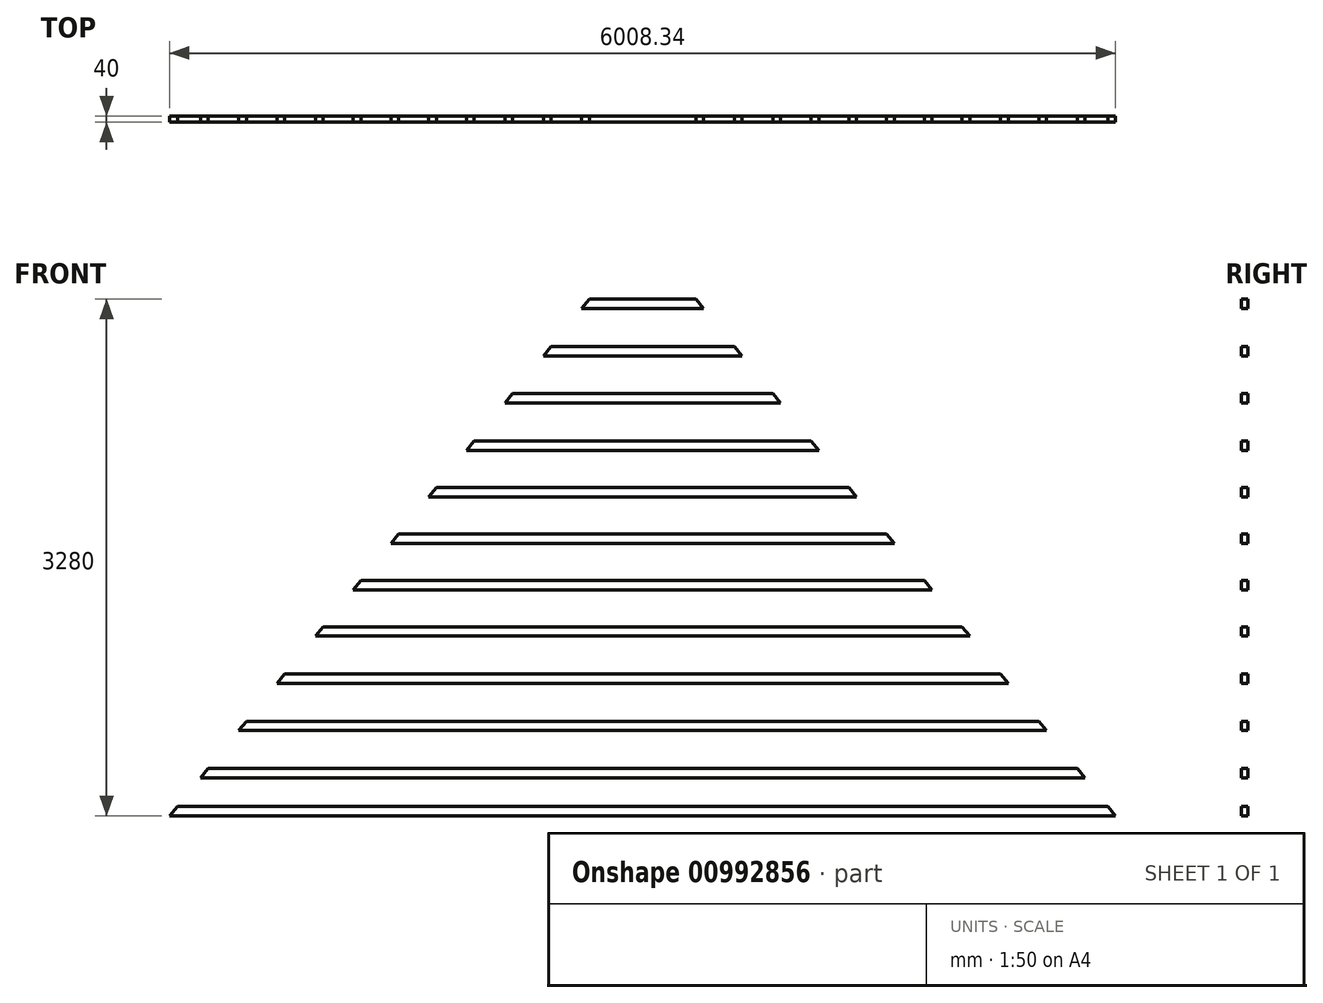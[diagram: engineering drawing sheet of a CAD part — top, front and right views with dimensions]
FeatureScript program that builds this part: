
annotation { "Feature Type Name" : "Feature", "Feature Type Description" : "" }
export const myFeature = defineFeature(function(context is Context, id is Id, definition is map)
    precondition{}
    {
        {
            var Q0;
            Q0=qCreatedBy(makeId("Front.planeOp"),FACE);
            var sketch = newSketch(context, id + "F0", { "sketchPlane" : qUnion([Q0])});
            skLineSegment(sketch, "E0", {"start": v(582.18, -714.87) * mm, "end": v(-582.6, -714.87) * mm});
            skLineSegment(sketch, "E1", {"start": v(630.94, -774.87) * mm, "end": v(-631.36, -774.87) * mm});
            skLineSegment(sketch, "E2", {"start": v(874.75, -1074.87) * mm, "end": v(-875.16, -1074.87) * mm});
            skLineSegment(sketch, "E3", {"start": v(3110.92, -3826.48) * mm, "end": v(-0.2, 1.76) * mm, "construction": true});
            skLineSegment(sketch, "E4", {"start": v(-3126.34, -3844.95) * mm, "end": v(-1118.97, -1374.87) * mm, "construction": true});
            skLineSegment(sketch, "E5", {"start": v(1069.79, -1314.87) * mm, "end": v(-1070.2, -1314.87) * mm});
            skLineSegment(sketch, "E6.trimOffspring", {"start": v(-0.2, 1.76) * mm, "end": v(-0.2, -4425.67) * mm, "construction": true});
            skLineSegment(sketch, "E7", {"start": v(-387.56, -474.87) * mm, "end": v(387.14, -474.87) * mm});
            skLineSegment(sketch, "E8", {"start": v(-0.2, -414.87) * mm, "end": v(338.38, -414.87) * mm});
            skLineSegment(sketch, "E9", {"start": v(-0.2, -414.87) * mm, "end": v(-338.8, -414.87) * mm});
            skLineSegment(sketch, "E10.trimOffspring", {"start": v(825.99, -1014.87) * mm, "end": v(-826.4, -1014.87) * mm});
            skLineSegment(sketch, "E11", {"start": v(-582.6, -714.87) * mm, "end": v(-631.36, -774.87) * mm});
            skLineSegment(sketch, "E12", {"start": v(582.18, -714.87) * mm, "end": v(630.94, -774.87) * mm});
            skLineSegment(sketch, "E13", {"start": v(-338.8, -414.87) * mm, "end": v(-387.56, -474.87) * mm});
            skLineSegment(sketch, "E14", {"start": v(338.38, -414.87) * mm, "end": v(387.14, -474.87) * mm});
            skPoint(sketch, "E15.trimOffspring.start.orphan", {"position": v(-0.2, -779.87) * mm});
            skLineSegment(sketch, "E16", {"start": v(825.99, -1014.87) * mm, "end": v(874.75, -1074.87) * mm});
            skLineSegment(sketch, "E17", {"start": v(-826.4, -1014.87) * mm, "end": v(-875.16, -1074.87) * mm});
            skLineSegment(sketch, "E18", {"start": v(1069.79, -1314.87) * mm, "end": v(1118.55, -1374.87) * mm});
            skLineSegment(sketch, "E19", {"start": v(-1070.2, -1314.87) * mm, "end": v(-1118.97, -1374.87) * mm});
            skLineSegment(sketch, "E20", {"start": v(-1118.97, -1374.87) * mm, "end": v(1118.55, -1374.87) * mm});
            skLineSegment(sketch, "E21.trimOffspring", {"start": v(-1118.97, -1374.87) * mm, "end": v(-0.2, 1.76) * mm, "construction": true});
            skLineSegment(sketch, "E22", {"start": v(-1309.94, -1609.87) * mm, "end": v(1309.53, -1609.87) * mm});
            skLineSegment(sketch, "E23", {"start": v(-1358.7, -1669.87) * mm, "end": v(1358.3, -1669.87) * mm});
            skLineSegment(sketch, "E24", {"start": v(-1358.7, -1669.87) * mm, "end": v(-1309.94, -1609.87) * mm});
            skLineSegment(sketch, "E25", {"start": v(1358.3, -1669.87) * mm, "end": v(1309.53, -1609.87) * mm});
            skLineSegment(sketch, "E26", {"start": v(-1598.45, -1964.87) * mm, "end": v(1598.03, -1964.87) * mm});
            skLineSegment(sketch, "E27", {"start": v(-1549.68, -1904.87) * mm, "end": v(1549.27, -1904.87) * mm});
            skLineSegment(sketch, "E28", {"start": v(1549.27, -1904.87) * mm, "end": v(1598.03, -1964.87) * mm});
            skLineSegment(sketch, "E29", {"start": v(-1598.45, -1964.87) * mm, "end": v(-1549.68, -1904.87) * mm});
            skLineSegment(sketch, "E30", {"start": v(-1789.42, -2199.87) * mm, "end": v(1789, -2199.87) * mm});
            skLineSegment(sketch, "E31", {"start": v(-1838.19, -2259.87) * mm, "end": v(1837.77, -2259.87) * mm});
            skLineSegment(sketch, "E32", {"start": v(1789, -2199.87) * mm, "end": v(1837.77, -2259.87) * mm});
            skLineSegment(sketch, "E33", {"start": v(-1789.42, -2199.87) * mm, "end": v(-1838.19, -2259.87) * mm});
            skLineSegment(sketch, "E34", {"start": v(-2029.16, -2494.87) * mm, "end": v(2028.75, -2494.87) * mm});
            skLineSegment(sketch, "E35", {"start": v(-2077.93, -2554.87) * mm, "end": v(2077.51, -2554.87) * mm});
            skLineSegment(sketch, "E36", {"start": v(-2029.16, -2494.87) * mm, "end": v(-2077.93, -2554.87) * mm, "construction": true});
            skLineSegment(sketch, "E37", {"start": v(2028.75, -2494.87) * mm, "end": v(2077.51, -2554.87) * mm, "construction": true});
            skLineSegment(sketch, "E38", {"start": v(-2272.97, -2794.87) * mm, "end": v(2272.55, -2794.87) * mm});
            skLineSegment(sketch, "E39", {"start": v(-2321.73, -2854.87) * mm, "end": v(2321.31, -2854.87) * mm});
            skPoint(sketch, "E40.orphan", {"position": v(-2233.68, -2854.87) * mm});
            skLineSegment(sketch, "E41", {"start": v(-2272.97, -2794.87) * mm, "end": v(-2321.73, -2854.87) * mm});
            skLineSegment(sketch, "E42", {"start": v(2272.55, -2794.87) * mm, "end": v(2321.31, -2854.87) * mm});
            skLineSegment(sketch, "E43", {"start": v(-2516.77, -3094.87) * mm, "end": v(2516.36, -3094.87) * mm});
            skLineSegment(sketch, "E44", {"start": v(-2565.53, -3154.87) * mm, "end": v(2565.12, -3154.87) * mm});
            skLineSegment(sketch, "E45", {"start": v(-2516.77, -3094.87) * mm, "end": v(-2565.53, -3154.87) * mm});
            skLineSegment(sketch, "E46", {"start": v(2516.36, -3094.87) * mm, "end": v(2565.12, -3154.87) * mm});
            skLineSegment(sketch, "E47", {"start": v(-2029.16, -2494.87) * mm, "end": v(-2077.93, -2554.87) * mm});
            skLineSegment(sketch, "E48", {"start": v(2028.75, -2494.87) * mm, "end": v(2077.51, -2554.87) * mm});
            skLineSegment(sketch, "E49", {"start": v(-2760.58, -3394.87) * mm, "end": v(2760.16, -3394.87) * mm});
            skLineSegment(sketch, "E50", {"start": v(-2809.34, -3454.87) * mm, "end": v(2808.92, -3454.87) * mm});
            skLineSegment(sketch, "E51", {"start": v(2760.16, -3394.87) * mm, "end": v(2808.92, -3454.87) * mm});
            skLineSegment(sketch, "E52", {"start": v(-2760.58, -3394.87) * mm, "end": v(-2809.34, -3454.87) * mm});
            skLineSegment(sketch, "E53", {"start": v(-2955.62, -3634.87) * mm, "end": v(2955.2, -3634.87) * mm});
            skLineSegment(sketch, "E54", {"start": v(-3004.38, -3694.87) * mm, "end": v(3003.96, -3694.87) * mm});
            skLineSegment(sketch, "E55", {"start": v(-3004.38, -3694.87) * mm, "end": v(-2955.62, -3634.87) * mm});
            skLineSegment(sketch, "E56", {"start": v(2955.2, -3634.87) * mm, "end": v(3003.96, -3694.87) * mm});
            skSolve(sketch);
        }
        {
            var Q0;
            Q0=makeQuery(id+"F0.imprint","IMPRINT",FACE,{"disambiguationData":[TD([[makeQuery(id+"F0.imprint","IMPRINT",EDGE,{"derivedFrom":sQuery(id+"F0.wireOp",EDGE,"E7")}),1.0]])]});
            var Q1;
            Q1=makeQuery(id+"F0.imprint","IMPRINT",FACE,{"disambiguationData":[TD([[makeQuery(id+"F0.imprint","IMPRINT",EDGE,{"derivedFrom":sQuery(id+"F0.wireOp",EDGE,"E0")}),1.0]])]});
            var Q2;
            Q2=makeQuery(id+"F0.imprint","IMPRINT",FACE,{"disambiguationData":[TD([[makeQuery(id+"F0.imprint","IMPRINT",EDGE,{"derivedFrom":sQuery(id+"F0.wireOp",EDGE,"E2")}),-1.0]])]});
            var Q3;
            Q3=makeQuery(id+"F0.imprint","IMPRINT",FACE,{"disambiguationData":[TD([[makeQuery(id+"F0.imprint","IMPRINT",EDGE,{"derivedFrom":sQuery(id+"F0.wireOp",EDGE,"E5")}),1.0]])]});
            var Q4;
            Q4=makeQuery(id+"F0.imprint","IMPRINT",FACE,{"disambiguationData":[TD([[makeQuery(id+"F0.imprint","IMPRINT",EDGE,{"derivedFrom":sQuery(id+"F0.wireOp",EDGE,"E22")}),-1.0]])]});
            var Q5;
            Q5=makeQuery(id+"F0.imprint","IMPRINT",FACE,{"disambiguationData":[TD([[makeQuery(id+"F0.imprint","IMPRINT",EDGE,{"derivedFrom":sQuery(id+"F0.wireOp",EDGE,"E26")}),1.0]])]});
            var Q6;
            Q6=makeQuery(id+"F0.imprint","IMPRINT",FACE,{"disambiguationData":[TD([[makeQuery(id+"F0.imprint","IMPRINT",EDGE,{"derivedFrom":sQuery(id+"F0.wireOp",EDGE,"E30")}),-1.0]])]});
            var Q7;
            Q7=makeQuery(id+"F0.imprint","IMPRINT",FACE,{"disambiguationData":[TD([[makeQuery(id+"F0.imprint","IMPRINT",EDGE,{"derivedFrom":sQuery(id+"F0.wireOp",EDGE,"E38")}),-1.0]])]});
            var Q8;
            Q8=makeQuery(id+"F0.imprint","IMPRINT",FACE,{"disambiguationData":[TD([[makeQuery(id+"F0.imprint","IMPRINT",EDGE,{"derivedFrom":sQuery(id+"F0.wireOp",EDGE,"E43")}),-1.0]])]});
            var Q9;
            Q9=makeQuery(id+"F0.imprint","IMPRINT",FACE,{"disambiguationData":[TD([[makeQuery(id+"F0.imprint","IMPRINT",EDGE,{"derivedFrom":sQuery(id+"F0.wireOp",EDGE,"E34")}),-1.0]])]});
            var Q10;
            Q10=makeQuery(id+"F0.imprint","IMPRINT",FACE,{"disambiguationData":[TD([[makeQuery(id+"F0.imprint","IMPRINT",EDGE,{"derivedFrom":sQuery(id+"F0.wireOp",EDGE,"E49")}),-1.0]])]});
            var Q11;
            Q11=makeQuery(id+"F0.imprint","IMPRINT",FACE,{"disambiguationData":[TD([[makeQuery(id+"F0.imprint","IMPRINT",EDGE,{"derivedFrom":sQuery(id+"F0.wireOp",EDGE,"E53")}),-1.0]])]});
            extrude(context, id + "F1", {"entities" : qUnion([Q0, Q1, Q2, Q3, Q4, Q5, Q6, Q7, Q8, Q9, Q10, Q11]), "depth" : 40 * mm, "offsetDistance" : 25 * mm});
        }
    });
